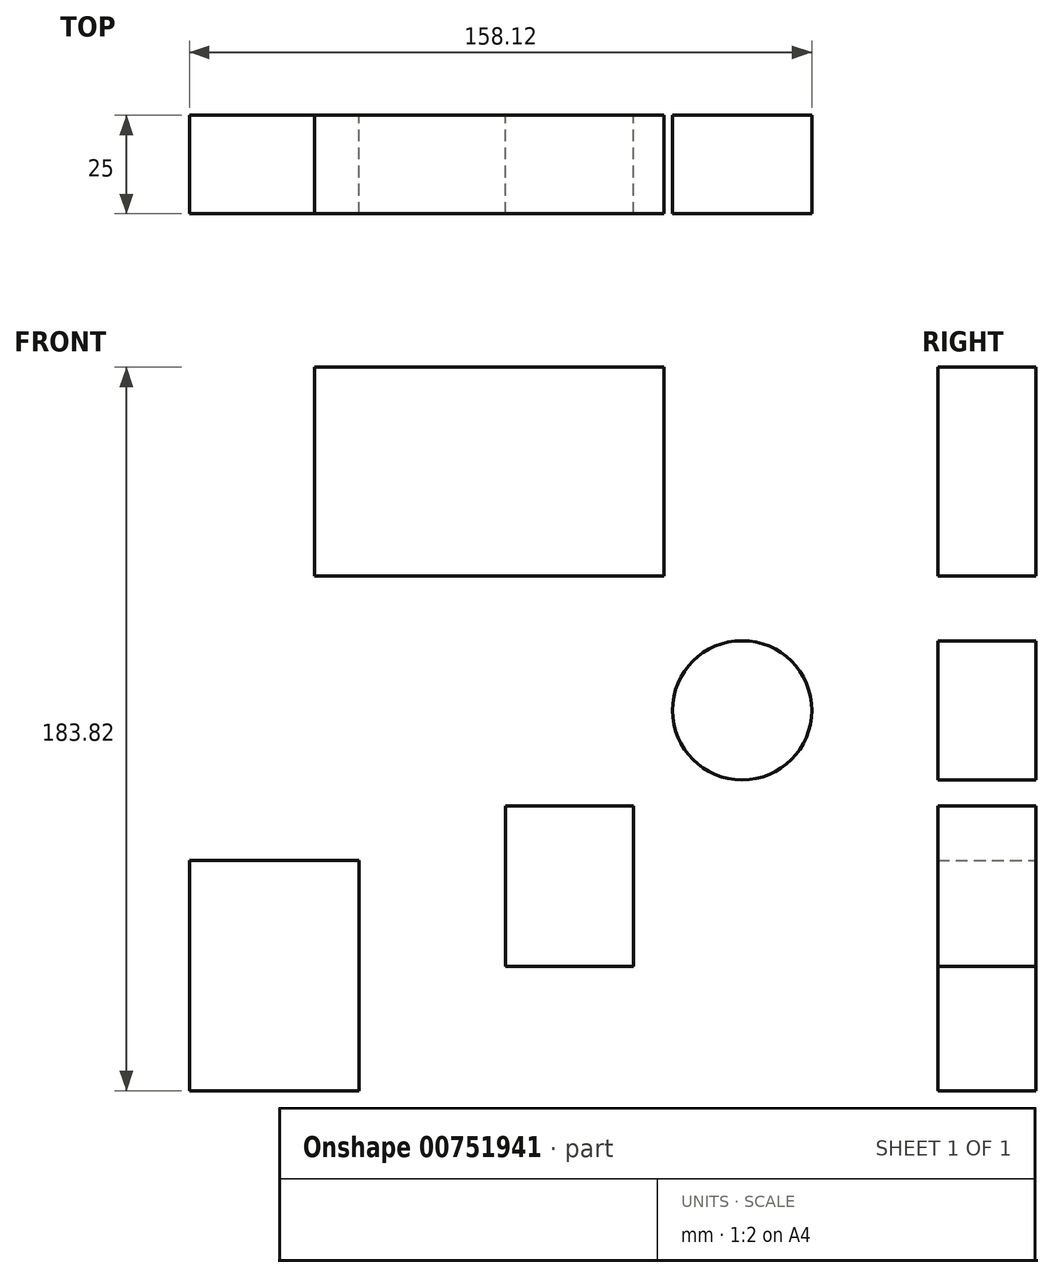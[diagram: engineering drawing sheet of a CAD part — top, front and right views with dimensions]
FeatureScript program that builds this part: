
annotation { "Feature Type Name" : "Feature", "Feature Type Description" : "" }
export const myFeature = defineFeature(function(context is Context, id is Id, definition is map)
    precondition{}
    {
        {
            var Q0;
            Q0=qCreatedBy(makeId("Front.planeOp"),FACE);
            var sketch = newSketch(context, id + "F0", { "sketchPlane" : qUnion([Q0])});
            skLineSegment(sketch, "E0.bottom", {"start": v(-18.65, 87.2) * mm, "end": v(70.15, 87.2) * mm});
            skLineSegment(sketch, "E0.top", {"start": v(-18.65, 34.1) * mm, "end": v(70.15, 34.1) * mm});
            skLineSegment(sketch, "E0.left", {"start": v(-18.65, 87.2) * mm, "end": v(-18.65, 34.1) * mm});
            skLineSegment(sketch, "E0.right", {"start": v(70.15, 87.2) * mm, "end": v(70.15, 34.1) * mm});
            skLineSegment(sketch, "E1.bottom", {"start": v(62.34, -24.33) * mm, "end": v(29.84, -24.33) * mm});
            skLineSegment(sketch, "E1.top", {"start": v(62.34, -65) * mm, "end": v(29.84, -65) * mm});
            skLineSegment(sketch, "E1.left", {"start": v(62.34, -24.33) * mm, "end": v(62.34, -65) * mm});
            skLineSegment(sketch, "E1.right", {"start": v(29.84, -24.33) * mm, "end": v(29.84, -65) * mm});
            skLineSegment(sketch, "E2.bottom", {"start": v(-7.28, -38.18) * mm, "end": v(-50.44, -38.18) * mm});
            skLineSegment(sketch, "E2.top", {"start": v(-7.28, -96.62) * mm, "end": v(-50.44, -96.62) * mm});
            skLineSegment(sketch, "E2.left", {"start": v(-7.28, -38.18) * mm, "end": v(-7.28, -96.62) * mm});
            skLineSegment(sketch, "E2.right", {"start": v(-50.44, -38.18) * mm, "end": v(-50.44, -96.62) * mm});
            skSolve(sketch);
        }
        {
            var Q0;
            Q0 = qSketchRegion(id + "F0", true);
            extrude(context, id + "F1", {"entities" : qUnion([Q0]), "depth" : 25 * mm, "offsetDistance" : 25 * mm});
        }
        {
            var Q0;
            Q0=qCreatedBy(makeId("Front.planeOp"),FACE);
            var sketch = newSketch(context, id + "F2", { "sketchPlane" : qUnion([Q0])});
            skCircle(sketch, "E3", {"center": v(90, 0) * mm, "radius": 17.69 * mm});
            skSolve(sketch);
        }
        {
            var Q0;
            Q0=makeQuery(id+"F2.imprint","IMPRINT",FACE,{"disambiguationData":[TD([[makeQuery(id+"F2.imprint","IMPRINT",EDGE,{"derivedFrom":sQuery(id+"F2.wireOp",EDGE,"E3")}),1.0]])]});
            extrude(context, id + "F3", {"entities" : qUnion([Q0]), "depth" : 25 * mm, "offsetDistance" : 25 * mm});
        }
    });
